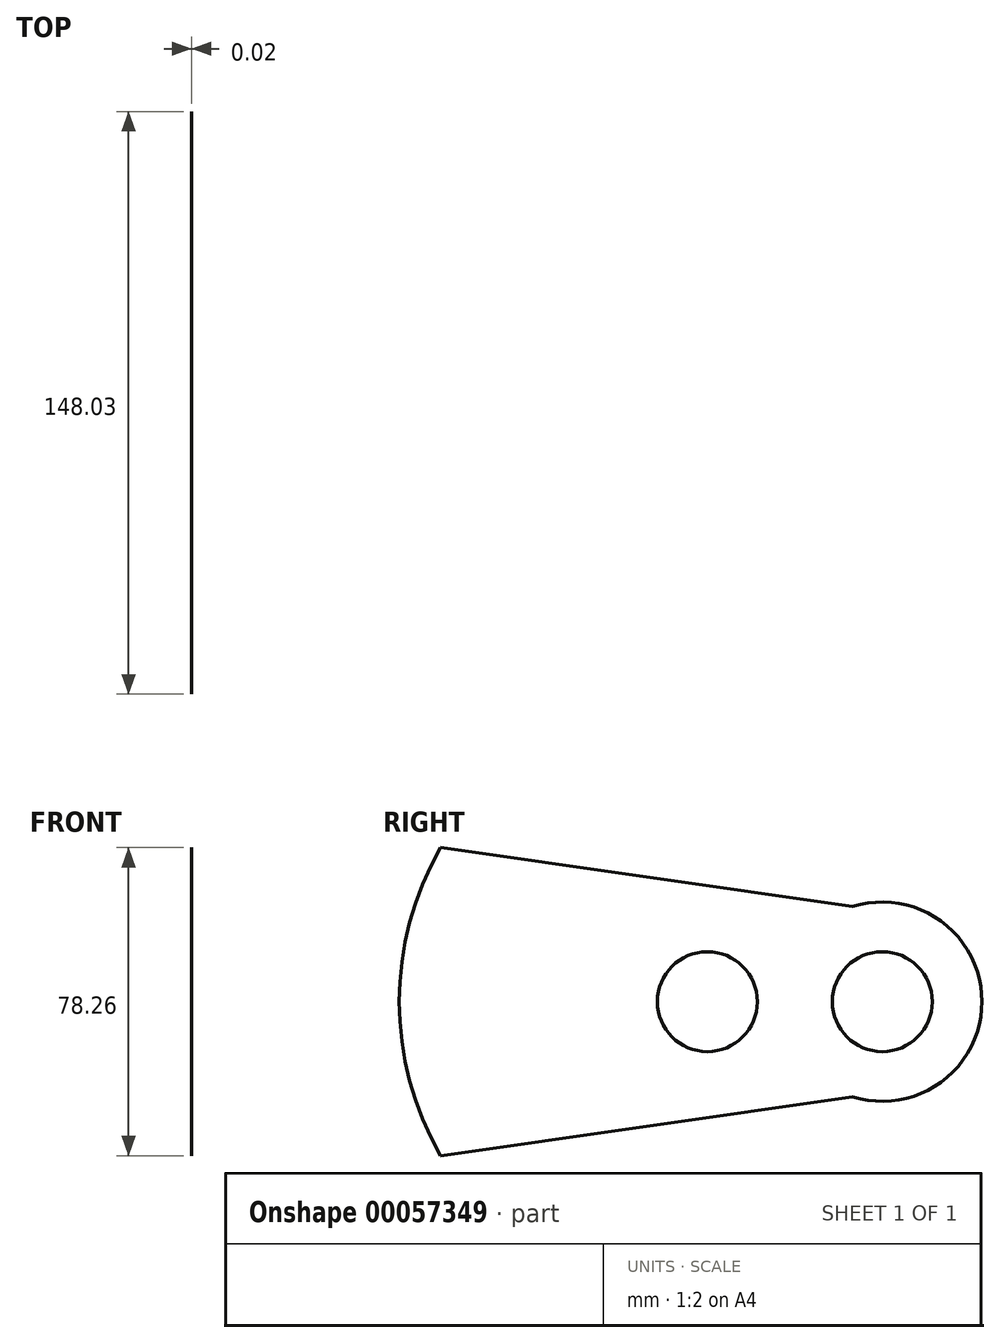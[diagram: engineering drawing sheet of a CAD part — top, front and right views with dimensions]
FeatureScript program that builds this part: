
annotation { "Feature Type Name" : "Feature", "Feature Type Description" : "" }
export const myFeature = defineFeature(function(context is Context, id is Id, definition is map)
    precondition{}
    {
        {
            var Q0;
            Q0=qCreatedBy(makeId("Right.planeOp"),FACE);
            var sketch = newSketch(context, id + "F0", { "sketchPlane" : qUnion([Q0])});
            skCircle(sketch, "E0", {"center": v(0, 0) * mm, "radius": 12.7 * mm});
            skCircle(sketch, "E1", {"center": v(44.45, 0) * mm, "radius": 12.7 * mm});
            skCircle(sketch, "E2", {"center": v(44.45, 0) * mm, "radius": 25.32 * mm});
            skLineSegment(sketch, "E3", {"start": v(36.9, 24.17) * mm, "end": v(-67.78, 39.13) * mm});
            skLineSegment(sketch, "E4.MirrorCS", {"start": v(36.9, -24.17) * mm, "end": v(-67.78, -39.13) * mm});
            skArc(sketch, "E5", {"start": v(-67.78, 39.13) * mm, "mid": v(-78.26, 0) * mm, "end": v(-67.78, -39.13) * mm});
            skLineSegment(sketch, "E6", {"start": v(36.9, 24.17) * mm, "end": v(36.9, -24.17) * mm, "construction": true});
            skLineSegment(sketch, "E7", {"start": v(-67.78, 39.13) * mm, "end": v(-67.78, -39.13) * mm, "construction": true});
            skSolve(sketch);
        }
        {
            var Q0;
            Q0=makeQuery(id+"F0.imprint","IMPRINT",FACE,{"disambiguationData":[TD([[makeQuery(id+"F0.imprint","IMPRINT",EDGE,{"derivedFrom":sQuery(id+"F0.wireOp",EDGE,"E0")}),-1.0]])]});
            var Q1;
            Q1=makeQuery(id+"F0.imprint","IMPRINT",FACE,{"disambiguationData":[TD([[makeQuery(id+"F0.imprint","IMPRINT",EDGE,{"derivedFrom":sQuery(id+"F0.wireOp",EDGE,"E1")}),-1.0]])]});
            extrude(context, id + "F1", {"entities" : qUnion([Q0, Q1]), "depth" : 1 / 50.8 * mm});
        }
    });
